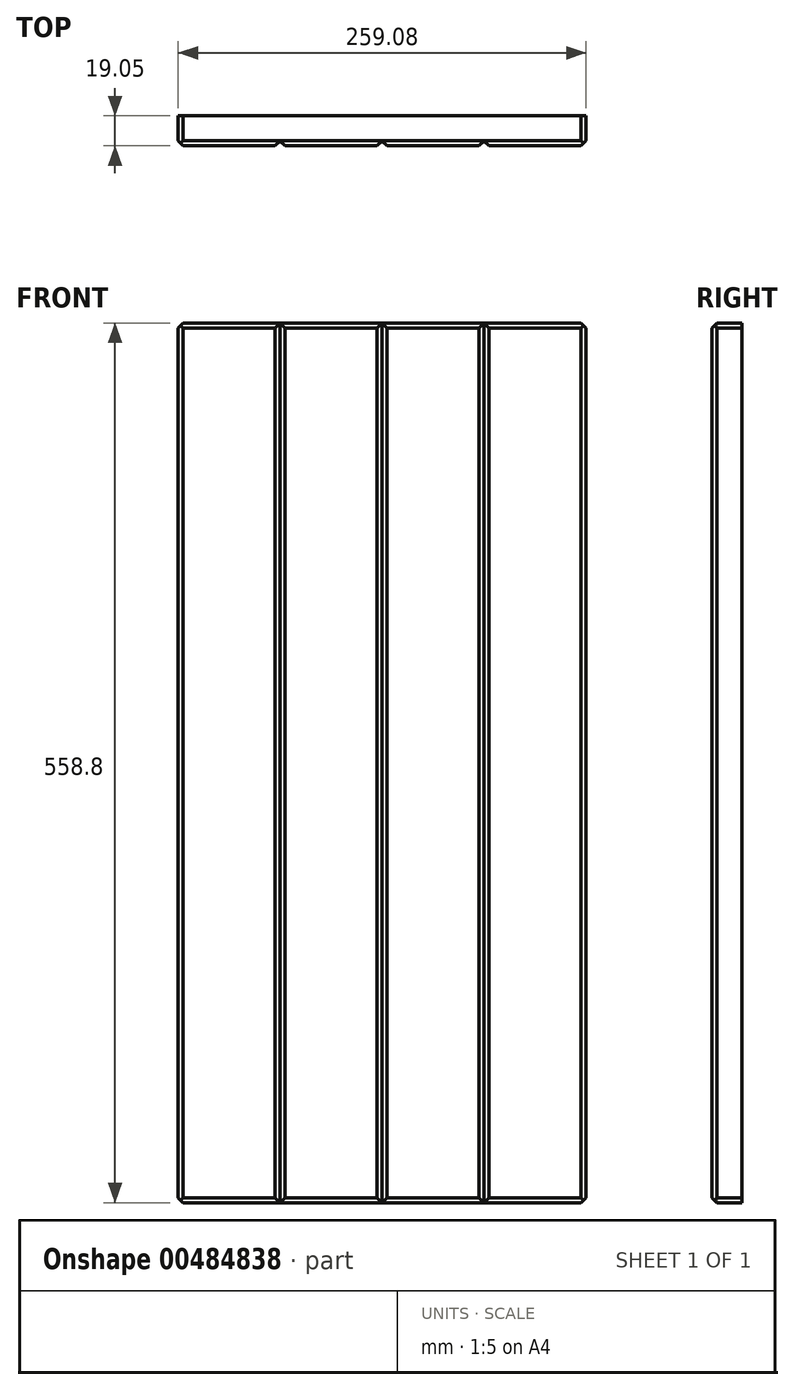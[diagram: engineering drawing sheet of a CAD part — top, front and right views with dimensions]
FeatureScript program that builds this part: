
annotation { "Feature Type Name" : "Feature", "Feature Type Description" : "" }
export const myFeature = defineFeature(function(context is Context, id is Id, definition is map)
    precondition{}
    {
        {
            var Q0;
            Q0=qCreatedBy(makeId("Front.planeOp"),FACE);
            var sketch = newSketch(context, id + "F0", { "sketchPlane" : qUnion([Q0])});
            skLineSegment(sketch, "E0.bottom", {"start": v(129.54, 279.4) * mm, "end": v(-129.54, 279.4) * mm});
            skLineSegment(sketch, "E0.top", {"start": v(129.54, -279.4) * mm, "end": v(-129.54, -279.4) * mm});
            skLineSegment(sketch, "E0.left", {"start": v(129.54, 279.4) * mm, "end": v(129.54, -279.4) * mm});
            skLineSegment(sketch, "E0.right", {"start": v(-129.54, 279.4) * mm, "end": v(-129.54, -279.4) * mm});
            skPoint(sketch, "E0.middle", {"position": v(0, 0) * mm});
            skSolve(sketch);
        }
        {
            var Q0;
            Q0 = qSketchRegion(id + "F0", true);
            extrude(context, id + "F1", {"entities" : qUnion([Q0]), "depth" : 19.05 * mm});
        }
        {
            var Q0;
            Q0=makeQuery(id+"F1.opExtrude","SWEPT_FACE",FACE,{"disambiguationData":[OSD([sQuery(id+"F0.wireOp",EDGE,"E0.top")])]});
            var sketch = newSketch(context, id + "F2", { "sketchPlane" : qUnion([Q0])});
            skLineSegment(sketch, "E1", {"start": v(-129.54, 19.05) * mm, "end": v(-64.77, 19.05) * mm});
            skLineSegment(sketch, "E2", {"start": v(-64.77, 19.05) * mm, "end": v(-67.94, 19.05) * mm});
            skLineSegment(sketch, "E3", {"start": v(-67.94, 19.05) * mm, "end": v(-64.77, 16.03) * mm});
            skLineSegment(sketch, "E4", {"start": v(-64.77, 19.05) * mm, "end": v(-61.6, 19.05) * mm});
            skLineSegment(sketch, "E5", {"start": v(-61.6, 19.05) * mm, "end": v(-64.77, 16.03) * mm});
            skLineSegment(sketch, "E6.1.0.0", {"start": v(3.18, 19.05) * mm, "end": v(0, 16.03) * mm});
            skLineSegment(sketch, "E6.1.0.1", {"start": v(0, 19.05) * mm, "end": v(3.18, 19.05) * mm});
            skLineSegment(sketch, "E6.1.0.2", {"start": v(-3.17, 19.05) * mm, "end": v(0, 16.03) * mm});
            skLineSegment(sketch, "E6.1.0.3", {"start": v(0, 19.05) * mm, "end": v(-3.17, 19.05) * mm});
            skLineSegment(sketch, "E6.2.0.0", {"start": v(67.95, 19.05) * mm, "end": v(64.77, 16.03) * mm});
            skLineSegment(sketch, "E6.2.0.1", {"start": v(64.77, 19.05) * mm, "end": v(67.95, 19.05) * mm});
            skLineSegment(sketch, "E6.2.0.2", {"start": v(61.6, 19.05) * mm, "end": v(64.77, 16.03) * mm});
            skLineSegment(sketch, "E6.2.0.3", {"start": v(64.77, 19.05) * mm, "end": v(61.6, 19.05) * mm});
            skSolve(sketch);
        }
        {
            var Q0;
            Q0 = qSketchRegion(id + "F2", true);
            extrude(context, id + "F3", {"entities" : qUnion([Q0]), "operationType" : NewBodyOperationType.REMOVE, "endBound" : BoundingType.THROUGH_ALL, "oppositeDirection" : true, "depth" : 25.4 * mm});
        }
        {
            var Q0;
            {var subQ0=sQuery(id+"F0.wireOp",EDGE,"E0.right");var subQ1=sQuery(id+"F0.wireOp",EDGE,"E0.top");Q0=makeQuery(id+"F3.boolean.opBoolean","SPLIT",EDGE,{"disambiguationData":[TD([makeQuery(id+"F1.opExtrude","SWEPT_FACE",FACE,{"disambiguationData":[OSD([subQ0])]})])],"derivedFrom":makeQuery(id+"F1.opExtrude","CAP_EDGE",EDGE,{"disambiguationData":[OSD([subQ1])],"isStart":false})});}
            var Q1;
            {var subQ0=sQuery(id+"F0.wireOp",EDGE,"E0.top");Q1=makeQuery(id+"F3.boolean.opBoolean","SPLIT",EDGE,{"disambiguationData":[TD([makeQuery(id+"F3.opExtrude","SWEPT_FACE",FACE,{"disambiguationData":[OSD([sQuery(id+"F2.wireOp",EDGE,"CAxPV77x-5upb-k8N2-m0mk-37POVM8K2Ngr")])]})])],"derivedFrom":makeQuery(id+"F1.opExtrude","CAP_EDGE",EDGE,{"disambiguationData":[OSD([subQ0])],"isStart":false})});}
            var Q2;
            {var subQ0=sQuery(id+"F0.wireOp",EDGE,"E0.top");Q2=makeQuery(id+"F3.boolean.opBoolean","SPLIT",EDGE,{"disambiguationData":[TD([makeQuery(id+"F3.opExtrude","SWEPT_FACE",FACE,{"disambiguationData":[OSD([sQuery(id+"F2.wireOp",EDGE,"oBDhtUpb-dP6W-yCmM-6fbA-jRnKg7Ga4u9I")])]})])],"derivedFrom":makeQuery(id+"F1.opExtrude","CAP_EDGE",EDGE,{"disambiguationData":[OSD([subQ0])],"isStart":false})});}
            var Q3;
            {var subQ0=sQuery(id+"F0.wireOp",EDGE,"E0.bottom");Q3=makeQuery(id+"F3.boolean.opBoolean","SPLIT",EDGE,{"disambiguationData":[TD([makeQuery(id+"F3.opExtrude","SWEPT_FACE",FACE,{"disambiguationData":[OSD([sQuery(id+"F2.wireOp",EDGE,"oBDhtUpb-dP6W-yCmM-6fbA-jRnKg7Ga4u9I")])]})])],"derivedFrom":makeQuery(id+"F1.opExtrude","CAP_EDGE",EDGE,{"disambiguationData":[OSD([subQ0])],"isStart":false})});}
            var Q4;
            {var subQ0=sQuery(id+"F0.wireOp",EDGE,"E0.bottom");Q4=makeQuery(id+"F3.boolean.opBoolean","SPLIT",EDGE,{"disambiguationData":[TD([makeQuery(id+"F3.opExtrude","SWEPT_FACE",FACE,{"disambiguationData":[OSD([sQuery(id+"F2.wireOp",EDGE,"CAxPV77x-5upb-k8N2-m0mk-37POVM8K2Ngr")])]})])],"derivedFrom":makeQuery(id+"F1.opExtrude","CAP_EDGE",EDGE,{"disambiguationData":[OSD([subQ0])],"isStart":false})});}
            var Q5;
            {var subQ0=sQuery(id+"F0.wireOp",EDGE,"E0.bottom");Q5=makeQuery(id+"F3.boolean.opBoolean","SPLIT",EDGE,{"disambiguationData":[TD([makeQuery(id+"F3.opExtrude","SWEPT_FACE",FACE,{"disambiguationData":[OSD([sQuery(id+"F2.wireOp",EDGE,"E5")])]})])],"derivedFrom":makeQuery(id+"F1.opExtrude","CAP_EDGE",EDGE,{"disambiguationData":[OSD([subQ0])],"isStart":false})});}
            var Q6;
            {var subQ0=sQuery(id+"F0.wireOp",EDGE,"E0.bottom");var subQ1=sQuery(id+"F0.wireOp",EDGE,"E0.right");Q6=makeQuery(id+"F3.boolean.opBoolean","SPLIT",EDGE,{"disambiguationData":[TD([makeQuery(id+"F1.opExtrude","SWEPT_FACE",FACE,{"disambiguationData":[OSD([subQ1])]})])],"derivedFrom":makeQuery(id+"F1.opExtrude","CAP_EDGE",EDGE,{"disambiguationData":[OSD([subQ0])],"isStart":false})});}
            var Q7;
            Q7=makeQuery(id+"F1.opExtrude","CAP_EDGE",EDGE,{"disambiguationData":[OSD([sQuery(id+"F0.wireOp",EDGE,"E0.right")])],"isStart":false});
            chamfer(context, id + "F4", {"entities" : qUnion([Q0, Q1, Q2, Q3, Q4, Q5, Q6, Q7]), "width" : 3.17 * mm, "tangentPropagation" : true});
        }
        {
            var Q0;
            Q0=makeQuery(id+"F1.opExtrude","SWEPT_EDGE",EDGE,{"disambiguationData":[OSD([sQuery(id+"F0.wireOp",EDGE,"E0.bottom"),sQuery(id+"F0.wireOp",EDGE,"E0.right")])]});
            var Q1;
            Q1=makeQuery(id+"F1.opExtrude","SWEPT_EDGE",EDGE,{"disambiguationData":[OSD([sQuery(id+"F0.wireOp",EDGE,"E0.bottom"),sQuery(id+"F0.wireOp",EDGE,"E0.left")])]});
            var Q2;
            Q2=makeQuery(id+"F1.opExtrude","SWEPT_EDGE",EDGE,{"disambiguationData":[OSD([sQuery(id+"F0.wireOp",EDGE,"E0.top"),sQuery(id+"F0.wireOp",EDGE,"E0.left")])]});
            var Q3;
            Q3=makeQuery(id+"F1.opExtrude","SWEPT_EDGE",EDGE,{"disambiguationData":[OSD([sQuery(id+"F0.wireOp",EDGE,"E0.top"),sQuery(id+"F0.wireOp",EDGE,"E0.right")])]});
            chamfer(context, id + "F5", {"entities" : qUnion([Q0, Q1, Q2, Q3]), "width" : 3.17 * mm, "tangentPropagation" : true});
        }
        {
            var Q0;
            Q0=makeQuery(id+"F1.opExtrude","CAP_EDGE",EDGE,{"disambiguationData":[OSD([sQuery(id+"F0.wireOp",EDGE,"E0.right")])],"isStart":false});
            var Q1;
            Q1=makeQuery(id+"F1.opExtrude","CAP_EDGE",EDGE,{"disambiguationData":[OSD([sQuery(id+"F0.wireOp",EDGE,"E0.left")])],"isStart":false});
            var Q2;
            {var subQ0=sQuery(id+"F0.wireOp",EDGE,"E0.bottom");var subQ1=sQuery(id+"F0.wireOp",EDGE,"E0.left");Q2=makeQuery(id+"F3.boolean.opBoolean","SPLIT",EDGE,{"disambiguationData":[TD([makeQuery(id+"F1.opExtrude","SWEPT_FACE",FACE,{"disambiguationData":[OSD([subQ1])]})])],"derivedFrom":makeQuery(id+"F1.opExtrude","CAP_EDGE",EDGE,{"disambiguationData":[OSD([subQ0])],"isStart":false})});}
            chamfer(context, id + "F6", {"entities" : qUnion([Q0, Q1, Q2]), "width" : 3.17 * mm, "tangentPropagation" : true});
        }
        {
            var Q0;
            {var subQ0=sQuery(id+"F0.wireOp",EDGE,"E0.bottom");var subQ1=sQuery(id+"F0.wireOp",EDGE,"E0.right");var subQ2=sQuery(id+"F0.wireOp",EDGE,"E0.top");Q0=makeQuery(id+"F3.boolean.opBoolean","SPLIT",FACE,{"disambiguationData":[TD([makeQuery(id+"F1.opExtrude","SWEPT_FACE",FACE,{"disambiguationData":[OSD([subQ1])]})])],"derivedFrom":makeQuery(id+"F1.opExtrude","CAP_FACE",FACE,{"disambiguationData":[OSD([subQ0,subQ2,sQuery(id+"F0.wireOp",EDGE,"E0.left"),subQ1])],"isStart":false})});}
            var sketch = newSketch(context, id + "F7", { "sketchPlane" : qUnion([Q0])});
            skLineSegment(sketch, "E7", {"start": v(-126.36, 276.23) * mm, "end": v(-126.36, 47.63) * mm});
            skLineSegment(sketch, "E8", {"start": v(-126.36, 47.63) * mm, "end": v(-95.88, 47.63) * mm});
            skLineSegment(sketch, "E9", {"start": v(95.82, 47.63) * mm, "end": v(126.3, 47.63) * mm});
            skLineSegment(sketch, "E10", {"start": v(126.3, 47.63) * mm, "end": v(95.82, 47.63) * mm});
            skPoint(sketch, "E11", {"position": v(95.82, 47.63) * mm});
            skPoint(sketch, "E12", {"position": v(-95.88, 47.63) * mm});
            skSolve(sketch);
        }
    });
